# Revit family: Water_Pressure_Reducing_Valves-Super_Capacity-WATTS-LFN223B_Series
name_source: partatom
category: Pipe Accessories
revit_build: Autodesk Revit 2014 (Build: 20130308_1515(x64)
units: mm (PartAtom-declared; Revit-internal decimal feet)

## types (2) — shared parameters
Country = United States
Description = Series LFN223B, LFN223BS Lead Free* High Capacity Water Pressure Reducing Valves are used in commercial, industrial, and institutional applications to reduce incoming water pressure for protection of plumbing system components and to reduce water consumption. It consists of a triple-coated corrosion preventative Lead Free* cast copper silicon alloy body construction, an enlarged diaphragm, spring cage and seat orifice for super capacity performance, sealed spring cage for waterworks pit installations and thermal expansion bypass.  Available with NPT threaded female inlet x NPT threaded female outlet with (LFN223BS) or without (LFN223B) strainer. Maximum Working Pressure: 300psi (21 bar), Adjustable Reduced Pressure Range: 25 to 75psi (172 to 517 kPa), Standard Pressure Setting: 50psi (345 kPa).
Flow Rate = See Specification Sheet
Installation Instructions = http://www.watts.com
Manufacturer = WATTS
Manufacturer Product Line = Water Safety & Flow Control
Material = Lead Free-WATTS-Cast Copper Silicon Alloy
Max. Working Pressure = 300psi (20.7 bar)
Model = LFN223B
Product Documentation Link = http://media.wattswater.com
Product Page URL = http://www.watts.com
Region = North America
URL = http://www.watts.com

## per-type parameters (varying)
- 2-1/2" LFN223B: Adjusting_Screw_Head_AC=0.43 "; Adjusting_Screw_Head_Hieght=-0.32 "; Adjusting_Screw_Hieght=1.8 "; Adjusting_Screw_Rad=0.249 "; Adjusting_Screw_WP=11.475 "; Body_Btm_Dist=2.1 "; Body_Fillet=1.19 "; Body_Hex_AC=2.02 "; Body_Hex_AF=1.75 "; Body_Hex_In_Dist=0.94 "; Body_Hex_Out_Dist=-0.94 "; Body_Rad=2.88 "; Btm_Plug_Dist=0.892 "; Btm_Plug_Rad=1.56 "; Cage_Boss_Hieght=0.31 "; Cage_Boss_Rad=0.568 "; Cage_Btm_Rad=3 "; Cage_Dist=3.115 "; Cage_Fillet=0.63 "; Cage_Flange_Rad=3.75 "; Cage_Flange_Thk=1.165 "; Cage_Hieght=6.25 "; Cage_Top_Rad=1.03 "; Connection Size=2.5 "; Connection Type=2-1/2" Female NPT; Connection_Rad=1"; Flow_Rad=1.66 "; In_Dist=3.89 "; In_Extrude_Dist=3.89 "; Length=7.875 "; Out_Dist=3.89 "; Out_Extrude_Dist=-3.89 "
- 3" LFN223B: Adjusting_Screw_Head_AC=0.86 "; Adjusting_Screw_Head_Hieght=-0.59 "; Adjusting_Screw_Hieght=3 "; Adjusting_Screw_Rad=0.495 "; Adjusting_Screw_WP=14.975 "; Body_Btm_Dist=2.92 "; Body_Fillet=0.12 "; Body_Hex_AC=2.74 "; Body_Hex_AF=2.375 "; Body_Hex_In_Dist=1.1 "; Body_Hex_Out_Dist=-1.1 "; Body_Rad=2.58 "; Btm_Plug_Dist=0.9 "; Btm_Plug_Rad=2.125 "; Cage_Boss_Hieght=0.93 "; Cage_Boss_Rad=1 "; Cage_Btm_Rad=3.75 "; Cage_Dist=3.785 "; Cage_Fillet=0.5 "; Cage_Flange_Rad=4.875 "; Cage_Flange_Thk=1.315 "; Cage_Hieght=7.26 "; Cage_Top_Rad=1.57 "; Connection Size=3 "; Connection Type=3" Female NPT; Connection_Rad=2"; Flow_Rad=2.375 "; In_Dist=5.32 "; In_Extrude_Dist=5.32 "; Length=10.5 "; Out_Dist=5.32 "; Out_Extrude_Dist=-5.32 "

## geometry (parser evidence)
native form markers: Sweep x1
no freeform markers — native parametric forms only
